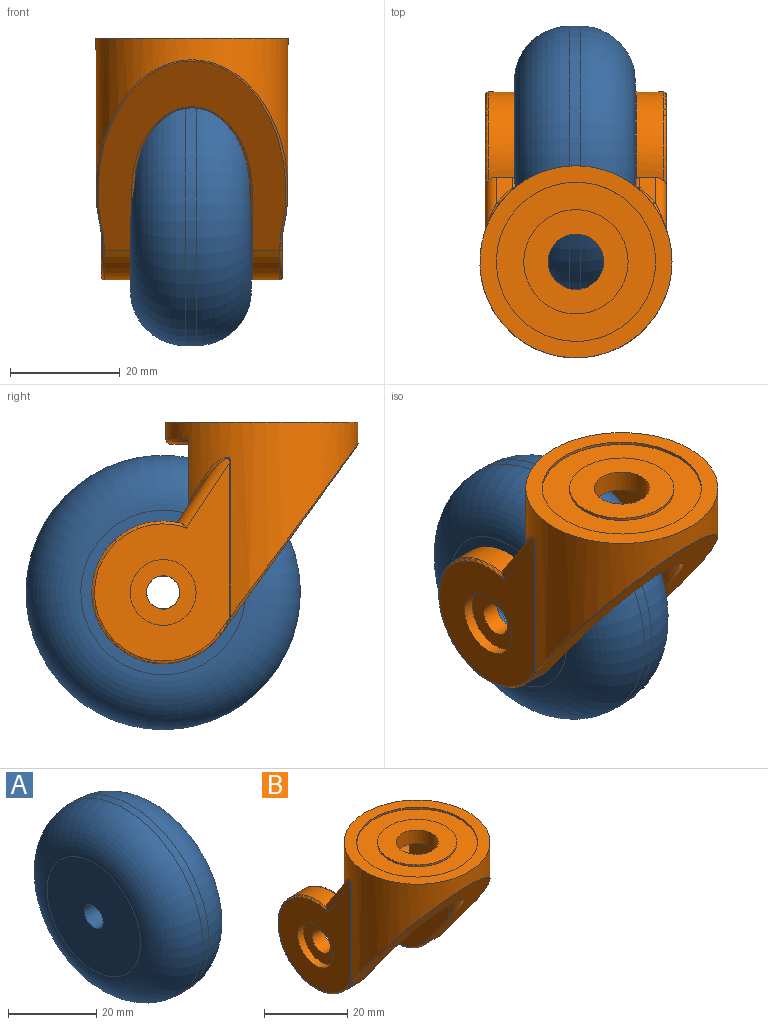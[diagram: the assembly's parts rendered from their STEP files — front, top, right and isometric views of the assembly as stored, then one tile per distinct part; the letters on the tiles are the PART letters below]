
ASSEMBLY  parts=2 mates=1
PART A: 6 faces, bbox 22x54.1x54.1 mm
  f0: cylinder r=3mm len=22mm, axis (-1,0,0), area 414.7mm2, adj f2,f3
  f1: cylinder r=25mm len=50mm, axis (-1,0,0), area 314.2mm2, adj f4,f5
  f2: plane 30x30mm, normal (1,0,0), area 678.6mm2, adj f0,f5
  f3: plane 30x30mm, normal (-1,0,0), area 678.6mm2, adj f0,f4
  f4: torus R=15mm, axis (1,0,0), area 2108.8mm2, adj f1,f3
  f5: torus R=15mm, axis (1,0,0), area 2108.8mm2, adj f1,f2
PART B: 59 faces, bbox 35.6x49.7x45.2 mm
  f0: plane 39.69x30.67mm, normal (-1,0,0), area 755.6mm2, adj f1,f4,f9,f26,f28,f36,f37,f38
  f1: cylinder r=3.05mm len=6.1mm, axis (-1,0,0), area 76.7mm2, adj f0,f22
  f2: cylinder r=3.05mm len=6.1mm, axis (-1,0,0), area 76.7mm2, adj f8,f20
  f3: plane 7.32x4.8mm, normal (0,0.84,0.55), area 17.4mm2, adj f18,f24,f44,f46
  f4: plane 27x21mm, normal (0,0,-1), area 414.5mm2, adj f0,f8,f9,f12,f51
  f5: plane 7.32x4.8mm, normal (0,0.84,0.55), area 17.4mm2, adj f19,f25,f37,f39
  f6: cylinder r=17.5mm len=35.32mm, axis (0,0,-1), area 1319.1mm2, adj f13,f35,f36,f39,f40,f41,f46,f47
  f7: plane 36.01x24.5mm, normal (-1,0,0), area 443mm2, adj f21,f24,f33,f34,f48
  f8: plane 39.52x30.51mm, normal (1,0,0), area 755.7mm2, adj f2,f4,f9,f27,f29,f35,f44,f45
  f9: cylinder r=10.5mm len=23.42mm, axis (0,0,1), area 452.7mm2, adj f0,f4,f8,f30
  f10: plane 36.01x24.5mm, normal (1,0,0), area 443mm2, adj f23,f25,f31,f32,f41
  f11: plane 19x19mm, normal (0,0,1), area 203.4mm2, adj f12,f14
  f12: cylinder r=5.05mm len=10.1mm, axis (0,0,-1), area 126.9mm2, adj f4,f11
  f13: plane 35x35mm, normal (0,0,1), area 301.6mm2, adj f6,f15
  f14: cylinder r=9.5mm len=19mm, axis (0,0,1), area 29.8mm2, adj f11,f16
  f15: cylinder r=14.5mm len=29mm, axis (0,0,1), area 45.6mm2, adj f13,f16
  f16: plane 29x29mm, normal (0,0,1), area 377mm2, adj f14,f15
  f17: plane 34.51x34.42mm, normal (0,-0.81,-0.59), area 606.7mm2, adj f18,f19,f28,f29,f30,f32,f34,f52
  f18: cylinder r=13mm len=26mm, axis (-1,0,0), area 279.1mm2, adj f3,f17,f24,f27,f33,f44
  f19: cylinder r=13mm len=26mm, axis (-1,0,0), area 279.1mm2, adj f5,f17,f25,f26,f31,f37
  f20: plane 12x12mm, normal (-1,0,0), area 83.9mm2, adj f2,f21
  f21: cylinder r=6mm len=12mm, axis (-1,0,0), area 75.4mm2, adj f7,f20
  f22: plane 12x12mm, normal (1,0,0), area 83.9mm2, adj f1,f23
  f23: cylinder r=6mm len=12mm, axis (1,0,0), area 75.4mm2, adj f10,f22
  f24: cylinder r=2mm len=13.52mm, axis (0,0.55,-0.84), area 40mm2, adj f3,f7,f18,f33,f47
  f25: cylinder r=2mm len=13.52mm, axis (0,-0.55,0.84), area 40mm2, adj f5,f10,f19,f31,f40
  f26: torus R=12.5mm, axis (-1,0,0), area 43.5mm2, adj f0,f19,f28,f37
  f27: torus R=12.5mm, axis (-1,0,0), area 43.5mm2, adj f8,f18,f29,f44
  f28: cylinder r=0.5mm len=11.19mm, axis (0,-0.59,0.81), area 10.6mm2, adj f0,f17,f26,f30
  f29: cylinder r=0.5mm len=11.19mm, axis (0,0.59,-0.81), area 10.6mm2, adj f8,f17,f27,f30
  f30: bspline ~22x15.52mm, area 48.4mm2, adj f9,f17,f28,f29
  f31: torus R=12.5mm, axis (-1,0,0), area 44.2mm2, adj f10,f19,f25,f32
  f32: cylinder r=0.5mm len=2.88mm, axis (0,0.59,-0.81), area 1.4mm2, adj f10,f17,f31,f42,f43
  f33: torus R=12.5mm, axis (-1,0,0), area 44.2mm2, adj f7,f18,f24,f34
  f34: cylinder r=0.5mm len=2.88mm, axis (0,-0.59,0.81), area 1.4mm2, adj f7,f17,f33,f49,f50
  f35: cylinder r=0.5mm len=11.38mm, axis (0,0,-1), area 12.4mm2, adj f6,f8,f45,f51
  f36: cylinder r=0.5mm len=11.38mm, axis (0,0,-1), area 12.4mm2, adj f0,f6,f38,f51
  f37: cylinder r=1mm len=3.43mm, axis (0,0.55,-0.84), area 5.2mm2, adj f0,f5,f19,f26,f38
  f38: bspline ~1.69x1.44mm, area 1.9mm2, adj f0,f36,f37,f39
  f39: bspline ~5.13x3.62mm, area 5.4mm2, adj f5,f6,f38,f40
  f40: bspline ~6.2x6.08mm, area 4.7mm2, adj f6,f25,f39,f41
  f41: cylinder r=1mm len=28.25mm, axis (0,0,-1), area 9.3mm2, adj f6,f10,f40,f42,f56
  f42: bspline ~0.72x0.54mm, area 0mm2, adj f32,f41,f43,f57
  f43: bspline ~2.82x1.89mm, area 0.1mm2, adj f32,f42,f58
  f44: cylinder r=1mm len=3.43mm, axis (0,-0.55,0.84), area 5.2mm2, adj f3,f8,f18,f27,f45
  f45: bspline ~1.69x1.44mm, area 1.9mm2, adj f8,f35,f44,f46
  f46: bspline ~5.13x3.62mm, area 5.4mm2, adj f3,f6,f45,f47
  f47: bspline ~6.2x6.08mm, area 4.7mm2, adj f6,f24,f46,f48
  f48: cylinder r=1mm len=28.25mm, axis (0,0,-1), area 9.3mm2, adj f6,f7,f47,f50,f54
  f49: bspline ~2.82x1.89mm, area 0.1mm2, adj f34,f50,f52
  f50: bspline ~0.72x0.54mm, area 0mm2, adj f34,f48,f49,f53
  f51: torus R=16.5mm, axis (0,0,1), area 36.8mm2, adj f0,f4,f6,f8,f35,f36
  f52: bspline ~1.96x1.28mm, area 0.4mm2, adj f17,f49,f53
  f53: bspline ~0.59x0.56mm, area 0.2mm2, adj f17,f50,f52,f54
  f54: bspline ~0.65x0.64mm, area 0.3mm2, adj f17,f48,f53,f55
  f55: bspline ~35.43x31.62mm, area 39.3mm2, adj f6,f17,f54,f56
  f56: bspline ~0.65x0.64mm, area 0.3mm2, adj f17,f41,f55,f57
  f57: bspline ~0.59x0.56mm, area 0.2mm2, adj f17,f42,f56,f58
  f58: bspline ~1.96x1.28mm, area 0.4mm2, adj f17,f43,f57
PLACE A t=(-12.01,41.52,6.13)mm
PLACE B t=(-11.81,-17.49,13.37)mm
MATE cylindrical A.f0 <-> B.f1  axis (1,0,0) through (-1.01,0.51,-13.63)mm
